# Revit family: NLRS_57_AIR_UN_steel wheather wall louvre bkvn exhaust LT_sacs
name_source: partatom
category: Air Terminals
revit_build: Autodesk Revit 2018 (Build: 20190510_1515(x64)
units: mm (PartAtom-declared; Revit-internal decimal feet)

## family parameters
Always vertical = No
Cut with Voids When Loaded = Yes
OmniClass Number = 23.75.70.21.27.11
OmniClass Title = Diffusers, Registers, and Grilles
Part Type = Normal
Room Calculation Point = Yes
Round Connector Dimension = Use Diameter
Shared = No
Work Plane-Based = No

## types (2) — shared parameters
Assembly Code = 57.0
Description = Solid Air weather louvre BKV (exhaust)
FireRating = 0
IfcDescription = Solid Air weather louvre BKV (exhaust)
IfcExportAs = IfcAirTerminal
IfcExportType = LOUVRE
IsExternal = No
LoadBearing = No
LookupTable = BKV
Manufacturer = Solid Air Climate Systems
Max Flow = 0.0 m³/h
Min Flow = 0.0 m³/h
Model = Weather louvre
NLRS_C_content_datum_uitgifte = 09-04-2021
NLRS_C_content_provider = Solid Air Climate Solutions
NLRS_C_content_versie = 3.18.01
NLRS_C_niveau ontwikkeling = LOD 400
SACS_Material_Frame = Sendzimir galvised steel
SACS_Show_Symbol = No
URL = https://solid-air.nl

## per-type parameters (varying)
| type | SACS_Base_Index | SACS_Factor_NDF1 | SACS_Factor_NDF2 | SACS_Factor_NDF3 | SACS_Factor_NDF4 | SACS_Factor_NDF5 | SACS_Factor_NDF6 | SACS_Material_Wire_mesh |
| BKVNGO | 1 | -1.574179 | -0.382208 | 2738.61 | -328633.2 | -164316.6 | 19717992 | 19x19mm galvanised |
| BKVNSO | 2 | -1.9823 | -0.444127 | 2053.9575 | -246474.9 | -123237.45 | 14788494 | 2x2 stainless steel |

## geometry (parser evidence)
native form markers: Sweep x10
no freeform markers — native parametric forms only
